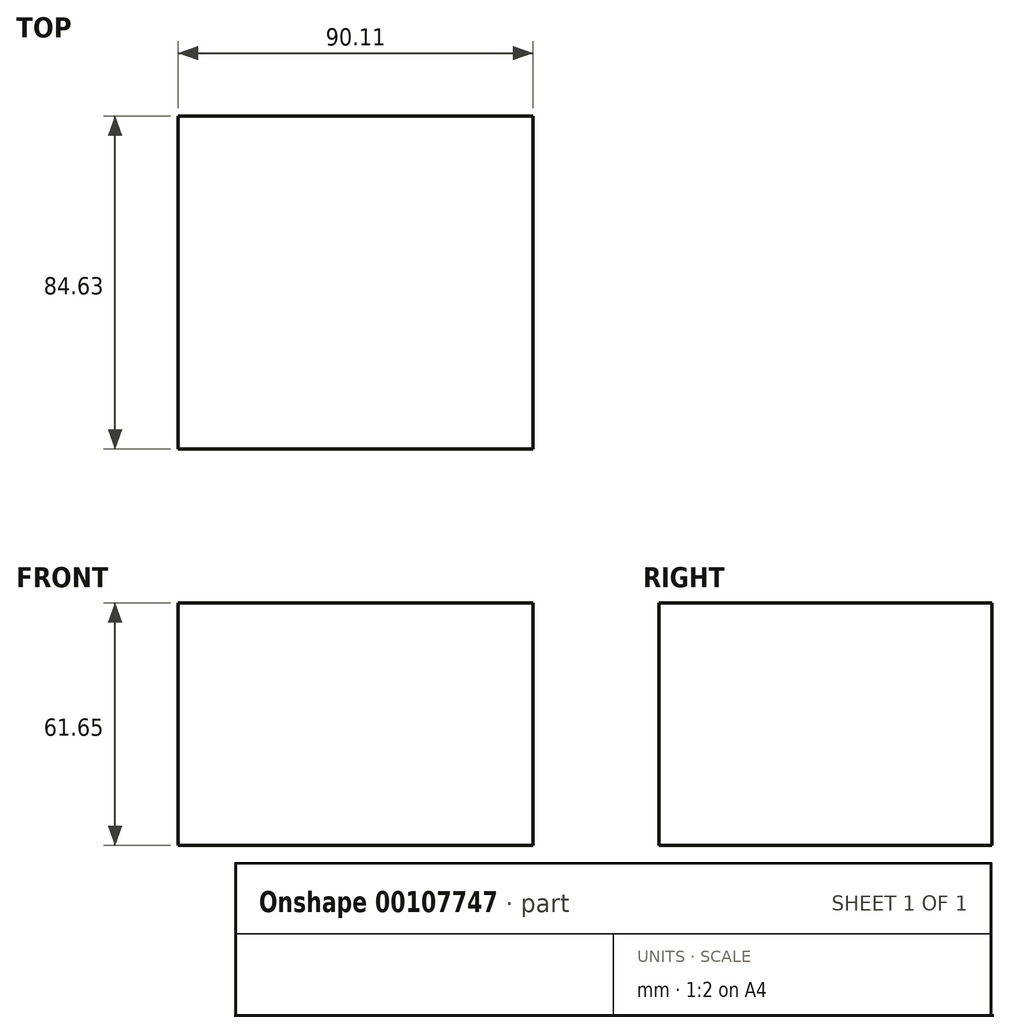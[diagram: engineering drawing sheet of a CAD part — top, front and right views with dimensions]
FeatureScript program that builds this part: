
annotation { "Feature Type Name" : "Feature", "Feature Type Description" : "" }
export const myFeature = defineFeature(function(context is Context, id is Id, definition is map)
    precondition{}
    {
        {
            var Q0;
            Q0=qCreatedBy(makeId("Top.planeOp"),FACE);
            var sketch = newSketch(context, id + "F0", { "sketchPlane" : qUnion([Q0])});
            skLineSegment(sketch, "E0.bottom", {"start": v(-46.87, 48.35) * mm, "end": v(43.24, 48.35) * mm});
            skLineSegment(sketch, "E0.top", {"start": v(-46.87, -36.28) * mm, "end": v(43.24, -36.28) * mm});
            skLineSegment(sketch, "E0.left", {"start": v(-46.87, 48.35) * mm, "end": v(-46.87, -36.28) * mm});
            skLineSegment(sketch, "E0.right", {"start": v(43.24, 48.35) * mm, "end": v(43.24, -36.28) * mm});
            skSolve(sketch);
        }
        {
            var Q0;
            Q0=makeQuery(id+"F0.imprint","IMPRINT",FACE,{"disambiguationData":[TD([[makeQuery(id+"F0.imprint","IMPRINT",EDGE,{"derivedFrom":sQuery(id+"F0.wireOp",EDGE,"E0.bottom")}),-1.0]])]});
            extrude(context, id + "F1", {"entities" : qUnion([Q0]), "depth" : 61.65 * mm});
        }
    });
